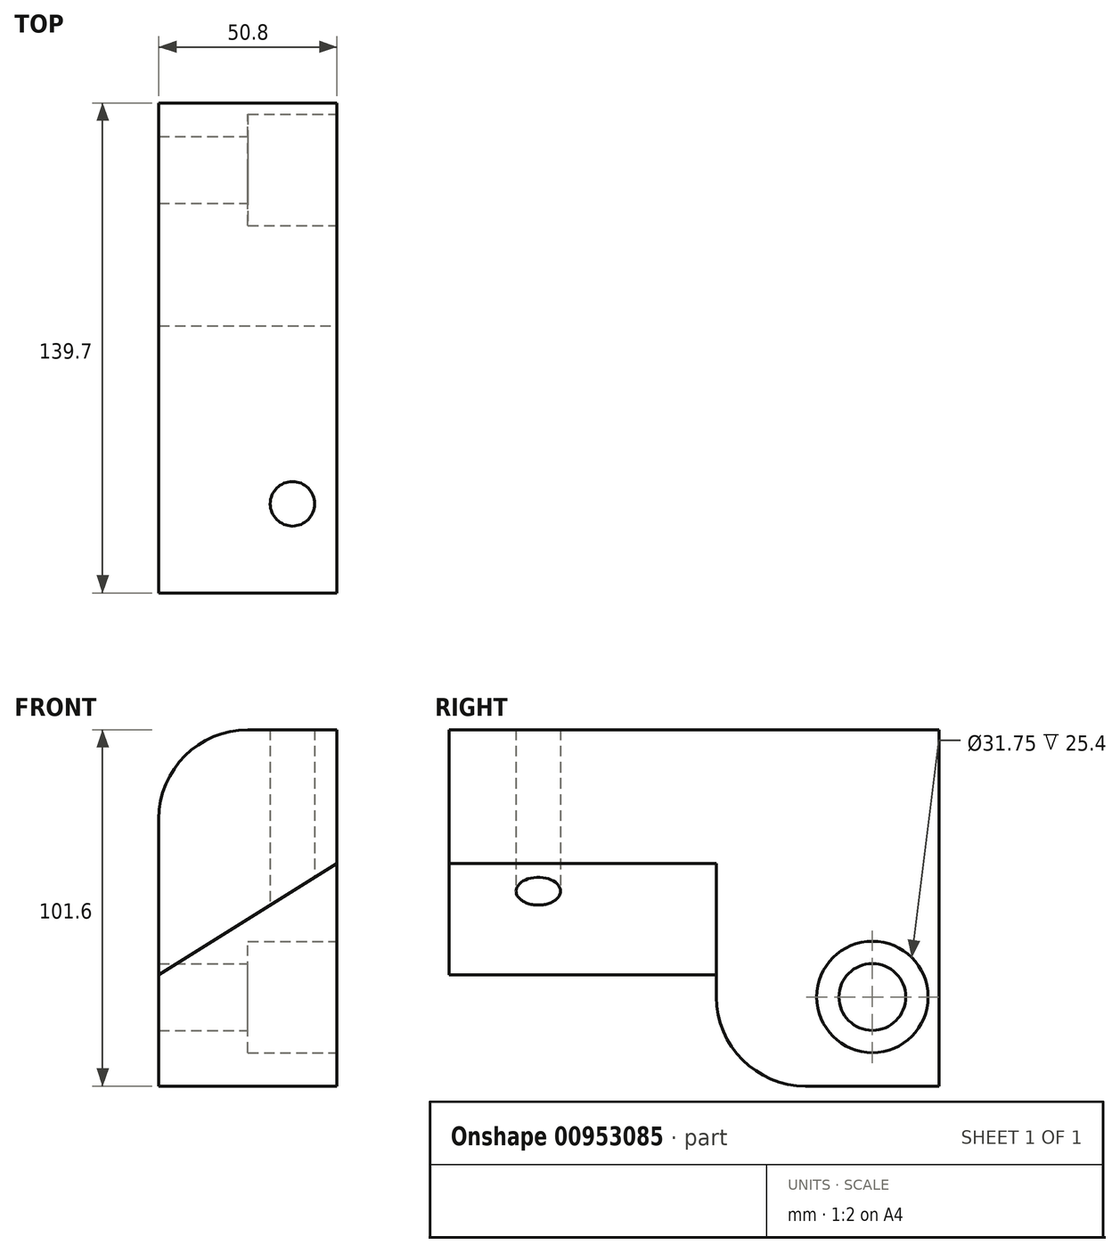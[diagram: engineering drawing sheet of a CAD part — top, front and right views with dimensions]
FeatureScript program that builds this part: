
annotation { "Feature Type Name" : "Feature", "Feature Type Description" : "" }
export const myFeature = defineFeature(function(context is Context, id is Id, definition is map)
    precondition{}
    {
        {
            var Q0;
            Q0=qCreatedBy(makeId("Front.planeOp"),FACE);
            var sketch = newSketch(context, id + "F0", { "sketchPlane" : qUnion([Q0])});
            skLineSegment(sketch, "E0", {"start": v(0, 0) * mm, "end": v(0, 76.2) * mm});
            skLineSegment(sketch, "E1", {"start": v(0, 0) * mm, "end": v(50.8, 0) * mm});
            skLineSegment(sketch, "E2", {"start": v(0, 25.4) * mm, "end": v(50.8, 25.4) * mm});
            skLineSegment(sketch, "E3", {"start": v(0, 31.75) * mm, "end": v(50.8, 63.5) * mm});
            skLineSegment(sketch, "E4", {"start": v(50.8, 63.5) * mm, "end": v(50.8, 0) * mm});
            skLineSegment(sketch, "E5", {"start": v(25.4, 101.6) * mm, "end": v(50.8, 101.6) * mm});
            skLineSegment(sketch, "E6", {"start": v(50.8, 101.6) * mm, "end": v(50.8, 63.5) * mm});
            skPoint(sketch, "E7.visualSharp", {"position": v(0, 101.6) * mm});
            skArc(sketch, "E7.filletArc", {"start": v(25.4, 101.6) * mm, "mid": v(7.44, 94.16) * mm, "end": v(0, 76.2) * mm});
            skSolve(sketch);
        }
        {
            var Q0;
            {var subQ0=sQuery(id+"F0.wireOp",EDGE,"E2");Q0=makeQuery(id+"F0.imprint","IMPRINT",FACE,{"disambiguationData":[TD([[makeQuery(id+"F0.imprint","IMPRINT",EDGE,{"derivedFrom":subQ0}),1.0]])]});}
            var Q1;
            {var subQ0=sQuery(id+"F0.wireOp",EDGE,"E1");Q1=makeQuery(id+"F0.imprint","IMPRINT",FACE,{"disambiguationData":[TD([[makeQuery(id+"F0.imprint","IMPRINT",EDGE,{"derivedFrom":subQ0}),1.0]])]});}
            var Q2;
            {var subQ0=sQuery(id+"F0.wireOp",EDGE,"E3");Q2=makeQuery(id+"F0.imprint","IMPRINT",FACE,{"disambiguationData":[TD([[makeQuery(id+"F0.imprint","IMPRINT",EDGE,{"derivedFrom":subQ0}),1.0]])]});}
            extrude(context, id + "F1", {"entities" : qUnion([Q0, Q1, Q2]), "depth" : 63.5 * mm, "offsetDistance" : 25.4 * mm});
        }
        {
            var Q0;
            {var subQ0=sQuery(id+"F0.wireOp",EDGE,"E3");Q0=makeQuery(id+"F0.imprint","IMPRINT",FACE,{"disambiguationData":[TD([[makeQuery(id+"F0.imprint","IMPRINT",EDGE,{"derivedFrom":subQ0}),1.0]])]});}
            extrude(context, id + "F2", {"entities" : qUnion([Q0]), "operationType" : NewBodyOperationType.ADD, "depth" : 139.7 * mm, "offsetDistance" : 25.4 * mm});
        }
        {
            var Q0;
            Q0=makeQuery(id+"F1.opExtrude","CAP_EDGE",EDGE,{"disambiguationData":[OSD([sQuery(id+"F0.wireOp",EDGE,"E1")])],"isStart":false});
            fillet(context, id + "F3", {"entities" : qUnion([Q0]), "radius" : 25.4 * mm, "tangentPropagation" : true, "allowEdgeOverflow" : false});
        }
        {
            var Q0;
            Q0=qCreatedBy(makeId("Top.planeOp"),FACE);
            var sketch = newSketch(context, id + "F4", { "sketchPlane" : qUnion([Q0])});
            skPoint(sketch, "E8", {"position": v(38.1, -114.3) * mm});
            skSolve(sketch);
        }
        {
            var Q0;
            Q0=sQuery(id+"F4.wireOp",VERTEX,"E8");
            var Q1;
            Q1=makeQuery(id+"F1.opExtrude","SWEPT_BODY",BODY,{"disambiguationData":[OSD([sQuery(id+"F0.wireOp",EDGE,"E0"),sQuery(id+"F0.wireOp",EDGE,"E1"),sQuery(id+"F0.wireOp",EDGE,"E4"),sQuery(id+"F0.wireOp",EDGE,"E5"),sQuery(id+"F0.wireOp",EDGE,"E6"),sQuery(id+"F0.wireOp",EDGE,"E7.filletArc")])]});
            hole(context, id + "F5", {"style" : HoleStyle.SIMPLE, "endStyle" : HoleEndStyle.THROUGH, "oppositeDirection" : true, "holeDiameter" : 12.7 * mm, "majorDiameter" : 6.35 * mm, "isTappedThrough" : true, "tappedDepth" : 12.7 * mm, "tapClearance" : 3, "locations" : qUnion([Q0]), "scope" : qUnion([Q1])});
        }
        {
            var Q0;
            {var subQ0=sQuery(id+"F0.wireOp",EDGE,"E6");Q0=makeQuery(id+"F2.boolean.opBoolean","MERGE",FACE,{"derivedFrom":[makeQuery(id+"F1.opExtrude","SWEPT_FACE",FACE,{"disambiguationData":[OSD([sQuery(id+"F0.wireOp",EDGE,"E4"),subQ0])]}),makeQuery(id+"F2.opExtrude","SWEPT_FACE",FACE,{"disambiguationData":[OSD([subQ0])]})]});}
            var sketch = newSketch(context, id + "F6", { "sketchPlane" : qUnion([Q0])});
            skPoint(sketch, "E9", {"position": v(-19.05, 25.4) * mm});
            skSolve(sketch);
        }
        {
            var Q0;
            Q0=sQuery(id+"F6.wireOp",VERTEX,"E9");
            var Q1;
            Q1=makeQuery(id+"F1.opExtrude","SWEPT_BODY",BODY,{"disambiguationData":[OSD([sQuery(id+"F0.wireOp",EDGE,"E0"),sQuery(id+"F0.wireOp",EDGE,"E1"),sQuery(id+"F0.wireOp",EDGE,"E4"),sQuery(id+"F0.wireOp",EDGE,"E5"),sQuery(id+"F0.wireOp",EDGE,"E6"),sQuery(id+"F0.wireOp",EDGE,"E7.filletArc")])]});
            hole(context, id + "F7", {"style" : HoleStyle.C_BORE, "endStyle" : HoleEndStyle.THROUGH, "holeDiameter" : 19.05 * mm, "cBoreDiameter" : 31.75 * mm, "cBoreDepth" : 25.4 * mm, "majorDiameter" : 6.35 * mm, "isTappedThrough" : true, "tappedDepth" : 12.7 * mm, "tapClearance" : 3, "locations" : qUnion([Q0]), "scope" : qUnion([Q1])});
        }
    });
